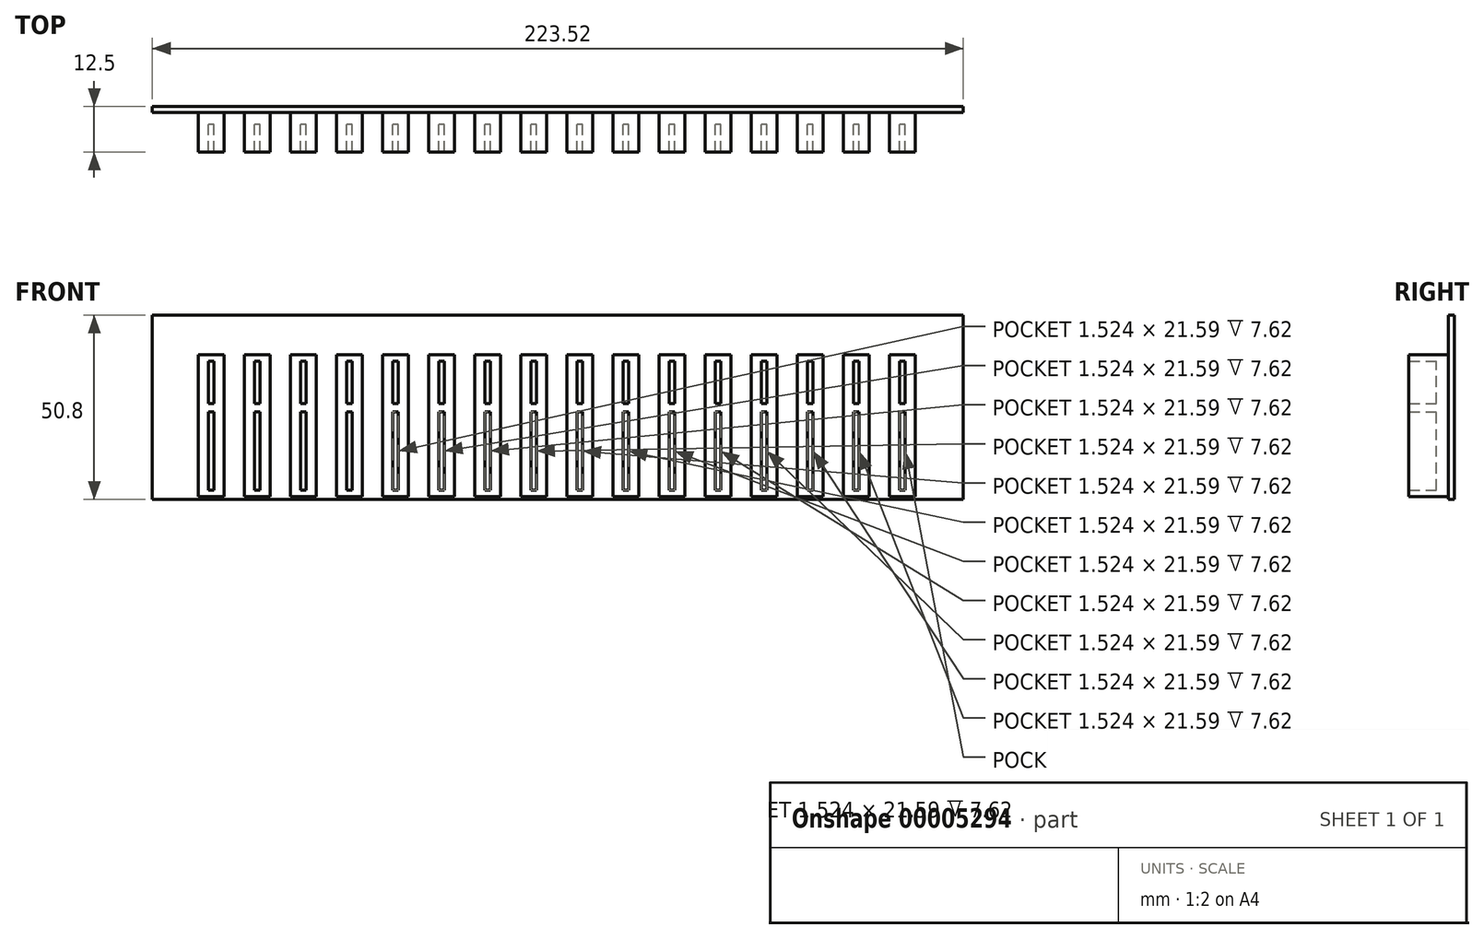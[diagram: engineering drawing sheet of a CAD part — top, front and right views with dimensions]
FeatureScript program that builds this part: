
annotation { "Feature Type Name" : "Feature", "Feature Type Description" : "" }
export const myFeature = defineFeature(function(context is Context, id is Id, definition is map)
    precondition{}
    {
        {
            var Q0;
            Q0=qCreatedBy(makeId("Front.planeOp"),FACE);
            var sketch = newSketch(context, id + "F0", { "sketchPlane" : qUnion([Q0])});
            skLineSegment(sketch, "E0.bottom", {"start": v(-92.93, 33.46) * mm, "end": v(130.6, 33.46) * mm});
            skLineSegment(sketch, "E0.top", {"start": v(-92.93, -17.34) * mm, "end": v(130.6, -17.34) * mm});
            skLineSegment(sketch, "E0.left", {"start": v(-92.93, 33.46) * mm, "end": v(-92.93, -17.34) * mm});
            skLineSegment(sketch, "E0.right", {"start": v(130.6, 33.46) * mm, "end": v(130.6, -17.34) * mm});
            skSolve(sketch);
        }
        {
            var Q0;
            Q0 = qSketchRegion(id + "F0", true);
            extrude(context, id + "F1", {"entities" : qUnion([Q0]), "depth" : 1.57 * mm});
        }
        {
            var Q0;
            Q0=makeQuery(id+"F1.opExtrude","CAP_FACE",FACE,{"disambiguationData":[OSD([sQuery(id+"F0.wireOp",EDGE,"E0.bottom"),sQuery(id+"F0.wireOp",EDGE,"E0.top"),sQuery(id+"F0.wireOp",EDGE,"E0.left"),sQuery(id+"F0.wireOp",EDGE,"E0.right")])],"isStart":false});
            var sketch = newSketch(context, id + "F2", { "sketchPlane" : qUnion([Q0])});
            skLineSegment(sketch, "E1", {"start": v(-80.23, 22.54) * mm, "end": v(-80.23, -16.58) * mm});
            skLineSegment(sketch, "E2", {"start": v(-80.23, 2.98) * mm, "end": v(-92.93, 2.98) * mm});
            skLineSegment(sketch, "E3", {"start": v(-80.23, 22.54) * mm, "end": v(-73.11, 22.54) * mm});
            skLineSegment(sketch, "E4", {"start": v(-73.11, 22.54) * mm, "end": v(-73.11, -16.58) * mm});
            skLineSegment(sketch, "E5", {"start": v(-73.11, -16.58) * mm, "end": v(-80.23, -16.58) * mm});
            skLineSegment(sketch, "E6", {"start": v(-76.67, 20.76) * mm, "end": v(-77.43, 20.76) * mm});
            skPoint(sketch, "E6.startSnap0", {"position": v(-76.67, 22.54) * mm});
            skLineSegment(sketch, "E7", {"start": v(-77.43, 20.76) * mm, "end": v(-77.43, 9.08) * mm});
            skLineSegment(sketch, "E8", {"start": v(-77.43, 9.08) * mm, "end": v(-75.9, 9.08) * mm});
            skLineSegment(sketch, "E9", {"start": v(-75.9, 9.08) * mm, "end": v(-75.9, 20.76) * mm});
            skLineSegment(sketch, "E10", {"start": v(-75.9, 20.76) * mm, "end": v(-76.67, 20.76) * mm});
            skLineSegment(sketch, "E11", {"start": v(-76.67, 20.76) * mm, "end": v(-76.67, 22.54) * mm});
            skLineSegment(sketch, "E12", {"start": v(-76.67, -16.58) * mm, "end": v(-76.67, -14.8) * mm});
            skLineSegment(sketch, "E13", {"start": v(-76.67, -14.8) * mm, "end": v(-77.43, -14.8) * mm});
            skLineSegment(sketch, "E14", {"start": v(-77.43, -14.8) * mm, "end": v(-77.43, 6.8) * mm});
            skLineSegment(sketch, "E15", {"start": v(-77.43, 6.8) * mm, "end": v(-75.9, 6.8) * mm});
            skLineSegment(sketch, "E16", {"start": v(-75.9, 6.8) * mm, "end": v(-75.9, -14.8) * mm});
            skLineSegment(sketch, "E17", {"start": v(-75.9, -14.8) * mm, "end": v(-76.67, -14.8) * mm});
            skLineSegment(sketch, "E18.1.0.0", {"start": v(-64.73, -14.8) * mm, "end": v(-64.73, 6.8) * mm});
            skPoint(sketch, "E18.1.0.1", {"position": v(-63.97, 22.54) * mm});
            skLineSegment(sketch, "E18.1.0.2", {"start": v(-63.2, 6.8) * mm, "end": v(-63.2, -14.8) * mm});
            skLineSegment(sketch, "E18.1.0.3", {"start": v(-67.53, 22.54) * mm, "end": v(-67.53, -16.58) * mm});
            skLineSegment(sketch, "E18.1.0.4", {"start": v(-67.53, 22.54) * mm, "end": v(-60.41, 22.54) * mm});
            skLineSegment(sketch, "E18.1.0.5", {"start": v(-60.41, 22.54) * mm, "end": v(-60.41, -16.58) * mm});
            skLineSegment(sketch, "E18.1.0.6", {"start": v(-60.41, -16.58) * mm, "end": v(-67.53, -16.58) * mm});
            skLineSegment(sketch, "E18.1.0.7", {"start": v(-63.2, 9.08) * mm, "end": v(-63.2, 20.76) * mm});
            skLineSegment(sketch, "E18.1.0.8", {"start": v(-64.73, 20.76) * mm, "end": v(-64.73, 9.08) * mm});
            skLineSegment(sketch, "E18.1.0.9", {"start": v(-63.97, -16.58) * mm, "end": v(-63.97, -14.8) * mm});
            skLineSegment(sketch, "E18.1.0.10", {"start": v(-64.73, 6.8) * mm, "end": v(-63.2, 6.8) * mm});
            skLineSegment(sketch, "E18.1.0.11", {"start": v(-63.97, 20.76) * mm, "end": v(-63.97, 22.54) * mm});
            skLineSegment(sketch, "E18.1.0.12", {"start": v(-64.73, 9.08) * mm, "end": v(-63.2, 9.08) * mm});
            skLineSegment(sketch, "E18.1.0.13", {"start": v(-63.97, -14.8) * mm, "end": v(-64.73, -14.8) * mm});
            skLineSegment(sketch, "E18.1.0.14", {"start": v(-63.2, -14.8) * mm, "end": v(-63.97, -14.8) * mm});
            skLineSegment(sketch, "E18.1.0.15", {"start": v(-63.2, 20.76) * mm, "end": v(-63.97, 20.76) * mm});
            skLineSegment(sketch, "E18.1.0.16", {"start": v(-63.97, 20.76) * mm, "end": v(-64.73, 20.76) * mm});
            skLineSegment(sketch, "E18.2.0.0", {"start": v(-52.03, -14.8) * mm, "end": v(-52.03, 6.8) * mm});
            skPoint(sketch, "E18.2.0.1", {"position": v(-51.27, 22.54) * mm});
            skLineSegment(sketch, "E18.2.0.2", {"start": v(-50.5, 6.8) * mm, "end": v(-50.5, -14.8) * mm});
            skLineSegment(sketch, "E18.2.0.3", {"start": v(-54.83, 22.54) * mm, "end": v(-54.83, -16.58) * mm});
            skLineSegment(sketch, "E18.2.0.4", {"start": v(-54.83, 22.54) * mm, "end": v(-47.71, 22.54) * mm});
            skLineSegment(sketch, "E18.2.0.5", {"start": v(-47.71, 22.54) * mm, "end": v(-47.71, -16.58) * mm});
            skLineSegment(sketch, "E18.2.0.6", {"start": v(-47.71, -16.58) * mm, "end": v(-54.83, -16.58) * mm});
            skLineSegment(sketch, "E18.2.0.7", {"start": v(-50.5, 9.08) * mm, "end": v(-50.5, 20.76) * mm});
            skLineSegment(sketch, "E18.2.0.8", {"start": v(-52.03, 20.76) * mm, "end": v(-52.03, 9.08) * mm});
            skLineSegment(sketch, "E18.2.0.9", {"start": v(-51.27, -16.58) * mm, "end": v(-51.27, -14.8) * mm});
            skLineSegment(sketch, "E18.2.0.10", {"start": v(-52.03, 6.8) * mm, "end": v(-50.5, 6.8) * mm});
            skLineSegment(sketch, "E18.2.0.11", {"start": v(-51.27, 20.76) * mm, "end": v(-51.27, 22.54) * mm});
            skLineSegment(sketch, "E18.2.0.12", {"start": v(-52.03, 9.08) * mm, "end": v(-50.5, 9.08) * mm});
            skLineSegment(sketch, "E18.2.0.13", {"start": v(-51.27, -14.8) * mm, "end": v(-52.03, -14.8) * mm});
            skLineSegment(sketch, "E18.2.0.14", {"start": v(-50.5, -14.8) * mm, "end": v(-51.27, -14.8) * mm});
            skLineSegment(sketch, "E18.2.0.15", {"start": v(-50.5, 20.76) * mm, "end": v(-51.27, 20.76) * mm});
            skLineSegment(sketch, "E18.2.0.16", {"start": v(-51.27, 20.76) * mm, "end": v(-52.03, 20.76) * mm});
            skLineSegment(sketch, "E18.3.0.0", {"start": v(-39.33, -14.8) * mm, "end": v(-39.33, 6.8) * mm});
            skPoint(sketch, "E18.3.0.1", {"position": v(-38.57, 22.54) * mm});
            skLineSegment(sketch, "E18.3.0.2", {"start": v(-37.8, 6.8) * mm, "end": v(-37.8, -14.8) * mm});
            skLineSegment(sketch, "E18.3.0.3", {"start": v(-42.13, 22.54) * mm, "end": v(-42.13, -16.58) * mm});
            skLineSegment(sketch, "E18.3.0.4", {"start": v(-42.13, 22.54) * mm, "end": v(-35.01, 22.54) * mm});
            skLineSegment(sketch, "E18.3.0.5", {"start": v(-35.01, 22.54) * mm, "end": v(-35.01, -16.58) * mm});
            skLineSegment(sketch, "E18.3.0.6", {"start": v(-35.01, -16.58) * mm, "end": v(-42.13, -16.58) * mm});
            skLineSegment(sketch, "E18.3.0.7", {"start": v(-37.8, 9.08) * mm, "end": v(-37.8, 20.76) * mm});
            skLineSegment(sketch, "E18.3.0.8", {"start": v(-39.33, 20.76) * mm, "end": v(-39.33, 9.08) * mm});
            skLineSegment(sketch, "E18.3.0.9", {"start": v(-38.57, -16.58) * mm, "end": v(-38.57, -14.8) * mm});
            skLineSegment(sketch, "E18.3.0.10", {"start": v(-39.33, 6.8) * mm, "end": v(-37.8, 6.8) * mm});
            skLineSegment(sketch, "E18.3.0.11", {"start": v(-38.57, 20.76) * mm, "end": v(-38.57, 22.54) * mm});
            skLineSegment(sketch, "E18.3.0.12", {"start": v(-39.33, 9.08) * mm, "end": v(-37.8, 9.08) * mm});
            skLineSegment(sketch, "E18.3.0.13", {"start": v(-38.57, -14.8) * mm, "end": v(-39.33, -14.8) * mm});
            skLineSegment(sketch, "E18.3.0.14", {"start": v(-37.8, -14.8) * mm, "end": v(-38.57, -14.8) * mm});
            skLineSegment(sketch, "E18.3.0.15", {"start": v(-37.8, 20.76) * mm, "end": v(-38.57, 20.76) * mm});
            skLineSegment(sketch, "E18.3.0.16", {"start": v(-38.57, 20.76) * mm, "end": v(-39.33, 20.76) * mm});
            skLineSegment(sketch, "E18.4.0.0", {"start": v(-26.63, -14.8) * mm, "end": v(-26.63, 6.8) * mm});
            skPoint(sketch, "E18.4.0.1", {"position": v(-25.87, 22.54) * mm});
            skLineSegment(sketch, "E18.4.0.2", {"start": v(-25.1, 6.8) * mm, "end": v(-25.1, -14.8) * mm});
            skLineSegment(sketch, "E18.4.0.3", {"start": v(-29.43, 22.54) * mm, "end": v(-29.43, -16.58) * mm});
            skLineSegment(sketch, "E18.4.0.4", {"start": v(-29.43, 22.54) * mm, "end": v(-22.31, 22.54) * mm});
            skLineSegment(sketch, "E18.4.0.5", {"start": v(-22.31, 22.54) * mm, "end": v(-22.31, -16.58) * mm});
            skLineSegment(sketch, "E18.4.0.6", {"start": v(-22.31, -16.58) * mm, "end": v(-29.43, -16.58) * mm});
            skLineSegment(sketch, "E18.4.0.7", {"start": v(-25.1, 9.08) * mm, "end": v(-25.1, 20.76) * mm});
            skLineSegment(sketch, "E18.4.0.8", {"start": v(-26.63, 20.76) * mm, "end": v(-26.63, 9.08) * mm});
            skLineSegment(sketch, "E18.4.0.9", {"start": v(-25.87, -16.58) * mm, "end": v(-25.87, -14.8) * mm});
            skLineSegment(sketch, "E18.4.0.10", {"start": v(-26.63, 6.8) * mm, "end": v(-25.1, 6.8) * mm});
            skLineSegment(sketch, "E18.4.0.11", {"start": v(-25.87, 20.76) * mm, "end": v(-25.87, 22.54) * mm});
            skLineSegment(sketch, "E18.4.0.12", {"start": v(-26.63, 9.08) * mm, "end": v(-25.1, 9.08) * mm});
            skLineSegment(sketch, "E18.4.0.13", {"start": v(-25.87, -14.8) * mm, "end": v(-26.63, -14.8) * mm});
            skLineSegment(sketch, "E18.4.0.14", {"start": v(-25.1, -14.8) * mm, "end": v(-25.87, -14.8) * mm});
            skLineSegment(sketch, "E18.4.0.15", {"start": v(-25.1, 20.76) * mm, "end": v(-25.87, 20.76) * mm});
            skLineSegment(sketch, "E18.4.0.16", {"start": v(-25.87, 20.76) * mm, "end": v(-26.63, 20.76) * mm});
            skLineSegment(sketch, "E18.5.0.0", {"start": v(-13.93, -14.8) * mm, "end": v(-13.93, 6.8) * mm});
            skPoint(sketch, "E18.5.0.1", {"position": v(-13.17, 22.54) * mm});
            skLineSegment(sketch, "E18.5.0.2", {"start": v(-12.4, 6.8) * mm, "end": v(-12.4, -14.8) * mm});
            skLineSegment(sketch, "E18.5.0.3", {"start": v(-16.73, 22.54) * mm, "end": v(-16.73, -16.58) * mm});
            skLineSegment(sketch, "E18.5.0.4", {"start": v(-16.73, 22.54) * mm, "end": v(-9.61, 22.54) * mm});
            skLineSegment(sketch, "E18.5.0.5", {"start": v(-9.61, 22.54) * mm, "end": v(-9.61, -16.58) * mm});
            skLineSegment(sketch, "E18.5.0.6", {"start": v(-9.61, -16.58) * mm, "end": v(-16.73, -16.58) * mm});
            skLineSegment(sketch, "E18.5.0.7", {"start": v(-12.4, 9.08) * mm, "end": v(-12.4, 20.76) * mm});
            skLineSegment(sketch, "E18.5.0.8", {"start": v(-13.93, 20.76) * mm, "end": v(-13.93, 9.08) * mm});
            skLineSegment(sketch, "E18.5.0.9", {"start": v(-13.17, -16.58) * mm, "end": v(-13.17, -14.8) * mm});
            skLineSegment(sketch, "E18.5.0.10", {"start": v(-13.93, 6.8) * mm, "end": v(-12.4, 6.8) * mm});
            skLineSegment(sketch, "E18.5.0.11", {"start": v(-13.17, 20.76) * mm, "end": v(-13.17, 22.54) * mm});
            skLineSegment(sketch, "E18.5.0.12", {"start": v(-13.93, 9.08) * mm, "end": v(-12.4, 9.08) * mm});
            skLineSegment(sketch, "E18.5.0.13", {"start": v(-13.17, -14.8) * mm, "end": v(-13.93, -14.8) * mm});
            skLineSegment(sketch, "E18.5.0.14", {"start": v(-12.4, -14.8) * mm, "end": v(-13.17, -14.8) * mm});
            skLineSegment(sketch, "E18.5.0.15", {"start": v(-12.4, 20.76) * mm, "end": v(-13.17, 20.76) * mm});
            skLineSegment(sketch, "E18.5.0.16", {"start": v(-13.17, 20.76) * mm, "end": v(-13.93, 20.76) * mm});
            skLineSegment(sketch, "E18.6.0.0", {"start": v(-1.23, -14.8) * mm, "end": v(-1.23, 6.8) * mm});
            skPoint(sketch, "E18.6.0.1", {"position": v(-0.47, 22.54) * mm});
            skLineSegment(sketch, "E18.6.0.2", {"start": v(0.3, 6.8) * mm, "end": v(0.3, -14.8) * mm});
            skLineSegment(sketch, "E18.6.0.3", {"start": v(-4.03, 22.54) * mm, "end": v(-4.03, -16.58) * mm});
            skLineSegment(sketch, "E18.6.0.4", {"start": v(-4.03, 22.54) * mm, "end": v(3.09, 22.54) * mm});
            skLineSegment(sketch, "E18.6.0.5", {"start": v(3.09, 22.54) * mm, "end": v(3.09, -16.58) * mm});
            skLineSegment(sketch, "E18.6.0.6", {"start": v(3.09, -16.58) * mm, "end": v(-4.03, -16.58) * mm});
            skLineSegment(sketch, "E18.6.0.7", {"start": v(0.3, 9.08) * mm, "end": v(0.3, 20.76) * mm});
            skLineSegment(sketch, "E18.6.0.8", {"start": v(-1.23, 20.76) * mm, "end": v(-1.23, 9.08) * mm});
            skLineSegment(sketch, "E18.6.0.9", {"start": v(-0.47, -16.58) * mm, "end": v(-0.47, -14.8) * mm});
            skLineSegment(sketch, "E18.6.0.10", {"start": v(-1.23, 6.8) * mm, "end": v(0.3, 6.8) * mm});
            skLineSegment(sketch, "E18.6.0.11", {"start": v(-0.47, 20.76) * mm, "end": v(-0.47, 22.54) * mm});
            skLineSegment(sketch, "E18.6.0.12", {"start": v(-1.23, 9.08) * mm, "end": v(0.3, 9.08) * mm});
            skLineSegment(sketch, "E18.6.0.13", {"start": v(-0.47, -14.8) * mm, "end": v(-1.23, -14.8) * mm});
            skLineSegment(sketch, "E18.6.0.14", {"start": v(0.3, -14.8) * mm, "end": v(-0.47, -14.8) * mm});
            skLineSegment(sketch, "E18.6.0.15", {"start": v(0.3, 20.76) * mm, "end": v(-0.47, 20.76) * mm});
            skLineSegment(sketch, "E18.6.0.16", {"start": v(-0.47, 20.76) * mm, "end": v(-1.23, 20.76) * mm});
            skLineSegment(sketch, "E18.7.0.0", {"start": v(11.47, -14.8) * mm, "end": v(11.47, 6.8) * mm});
            skPoint(sketch, "E18.7.0.1", {"position": v(12.23, 22.54) * mm});
            skLineSegment(sketch, "E18.7.0.2", {"start": v(13, 6.8) * mm, "end": v(13, -14.8) * mm});
            skLineSegment(sketch, "E18.7.0.3", {"start": v(8.67, 22.54) * mm, "end": v(8.67, -16.58) * mm});
            skLineSegment(sketch, "E18.7.0.4", {"start": v(8.67, 22.54) * mm, "end": v(15.79, 22.54) * mm});
            skLineSegment(sketch, "E18.7.0.5", {"start": v(15.79, 22.54) * mm, "end": v(15.79, -16.58) * mm});
            skLineSegment(sketch, "E18.7.0.6", {"start": v(15.79, -16.58) * mm, "end": v(8.67, -16.58) * mm});
            skLineSegment(sketch, "E18.7.0.7", {"start": v(13, 9.08) * mm, "end": v(13, 20.76) * mm});
            skLineSegment(sketch, "E18.7.0.8", {"start": v(11.47, 20.76) * mm, "end": v(11.47, 9.08) * mm});
            skLineSegment(sketch, "E18.7.0.9", {"start": v(12.23, -16.58) * mm, "end": v(12.23, -14.8) * mm});
            skLineSegment(sketch, "E18.7.0.10", {"start": v(11.47, 6.8) * mm, "end": v(13, 6.8) * mm});
            skLineSegment(sketch, "E18.7.0.11", {"start": v(12.23, 20.76) * mm, "end": v(12.23, 22.54) * mm});
            skLineSegment(sketch, "E18.7.0.12", {"start": v(11.47, 9.08) * mm, "end": v(13, 9.08) * mm});
            skLineSegment(sketch, "E18.7.0.13", {"start": v(12.23, -14.8) * mm, "end": v(11.47, -14.8) * mm});
            skLineSegment(sketch, "E18.7.0.14", {"start": v(13, -14.8) * mm, "end": v(12.23, -14.8) * mm});
            skLineSegment(sketch, "E18.7.0.15", {"start": v(13, 20.76) * mm, "end": v(12.23, 20.76) * mm});
            skLineSegment(sketch, "E18.7.0.16", {"start": v(12.23, 20.76) * mm, "end": v(11.47, 20.76) * mm});
            skLineSegment(sketch, "E18.8.0.0", {"start": v(24.17, -14.8) * mm, "end": v(24.17, 6.8) * mm});
            skPoint(sketch, "E18.8.0.1", {"position": v(24.93, 22.54) * mm});
            skLineSegment(sketch, "E18.8.0.2", {"start": v(25.7, 6.8) * mm, "end": v(25.7, -14.8) * mm});
            skLineSegment(sketch, "E18.8.0.3", {"start": v(21.37, 22.54) * mm, "end": v(21.37, -16.58) * mm});
            skLineSegment(sketch, "E18.8.0.4", {"start": v(21.37, 22.54) * mm, "end": v(28.49, 22.54) * mm});
            skLineSegment(sketch, "E18.8.0.5", {"start": v(28.49, 22.54) * mm, "end": v(28.49, -16.58) * mm});
            skLineSegment(sketch, "E18.8.0.6", {"start": v(28.49, -16.58) * mm, "end": v(21.37, -16.58) * mm});
            skLineSegment(sketch, "E18.8.0.7", {"start": v(25.7, 9.08) * mm, "end": v(25.7, 20.76) * mm});
            skLineSegment(sketch, "E18.8.0.8", {"start": v(24.17, 20.76) * mm, "end": v(24.17, 9.08) * mm});
            skLineSegment(sketch, "E18.8.0.9", {"start": v(24.93, -16.58) * mm, "end": v(24.93, -14.8) * mm});
            skLineSegment(sketch, "E18.8.0.10", {"start": v(24.17, 6.8) * mm, "end": v(25.7, 6.8) * mm});
            skLineSegment(sketch, "E18.8.0.11", {"start": v(24.93, 20.76) * mm, "end": v(24.93, 22.54) * mm});
            skLineSegment(sketch, "E18.8.0.12", {"start": v(24.17, 9.08) * mm, "end": v(25.7, 9.08) * mm});
            skLineSegment(sketch, "E18.8.0.13", {"start": v(24.93, -14.8) * mm, "end": v(24.17, -14.8) * mm});
            skLineSegment(sketch, "E18.8.0.14", {"start": v(25.7, -14.8) * mm, "end": v(24.93, -14.8) * mm});
            skLineSegment(sketch, "E18.8.0.15", {"start": v(25.7, 20.76) * mm, "end": v(24.93, 20.76) * mm});
            skLineSegment(sketch, "E18.8.0.16", {"start": v(24.93, 20.76) * mm, "end": v(24.17, 20.76) * mm});
            skLineSegment(sketch, "E18.9.0.0", {"start": v(36.87, -14.8) * mm, "end": v(36.87, 6.8) * mm});
            skPoint(sketch, "E18.9.0.1", {"position": v(37.63, 22.54) * mm});
            skLineSegment(sketch, "E18.9.0.2", {"start": v(38.4, 6.8) * mm, "end": v(38.4, -14.8) * mm});
            skLineSegment(sketch, "E18.9.0.3", {"start": v(34.07, 22.54) * mm, "end": v(34.07, -16.58) * mm});
            skLineSegment(sketch, "E18.9.0.4", {"start": v(34.07, 22.54) * mm, "end": v(41.19, 22.54) * mm});
            skLineSegment(sketch, "E18.9.0.5", {"start": v(41.19, 22.54) * mm, "end": v(41.19, -16.58) * mm});
            skLineSegment(sketch, "E18.9.0.6", {"start": v(41.19, -16.58) * mm, "end": v(34.07, -16.58) * mm});
            skLineSegment(sketch, "E18.9.0.7", {"start": v(38.4, 9.08) * mm, "end": v(38.4, 20.76) * mm});
            skLineSegment(sketch, "E18.9.0.8", {"start": v(36.87, 20.76) * mm, "end": v(36.87, 9.08) * mm});
            skLineSegment(sketch, "E18.9.0.9", {"start": v(37.63, -16.58) * mm, "end": v(37.63, -14.8) * mm});
            skLineSegment(sketch, "E18.9.0.10", {"start": v(36.87, 6.8) * mm, "end": v(38.4, 6.8) * mm});
            skLineSegment(sketch, "E18.9.0.11", {"start": v(37.63, 20.76) * mm, "end": v(37.63, 22.54) * mm});
            skLineSegment(sketch, "E18.9.0.12", {"start": v(36.87, 9.08) * mm, "end": v(38.4, 9.08) * mm});
            skLineSegment(sketch, "E18.9.0.13", {"start": v(37.63, -14.8) * mm, "end": v(36.87, -14.8) * mm});
            skLineSegment(sketch, "E18.9.0.14", {"start": v(38.4, -14.8) * mm, "end": v(37.63, -14.8) * mm});
            skLineSegment(sketch, "E18.9.0.15", {"start": v(38.4, 20.76) * mm, "end": v(37.63, 20.76) * mm});
            skLineSegment(sketch, "E18.9.0.16", {"start": v(37.63, 20.76) * mm, "end": v(36.87, 20.76) * mm});
            skLineSegment(sketch, "E18.10.0.0", {"start": v(49.57, -14.8) * mm, "end": v(49.57, 6.8) * mm});
            skPoint(sketch, "E18.10.0.1", {"position": v(50.33, 22.54) * mm});
            skLineSegment(sketch, "E18.10.0.2", {"start": v(51.1, 6.8) * mm, "end": v(51.1, -14.8) * mm});
            skLineSegment(sketch, "E18.10.0.3", {"start": v(46.77, 22.54) * mm, "end": v(46.77, -16.58) * mm});
            skLineSegment(sketch, "E18.10.0.4", {"start": v(46.77, 22.54) * mm, "end": v(53.89, 22.54) * mm});
            skLineSegment(sketch, "E18.10.0.5", {"start": v(53.89, 22.54) * mm, "end": v(53.89, -16.58) * mm});
            skLineSegment(sketch, "E18.10.0.6", {"start": v(53.89, -16.58) * mm, "end": v(46.77, -16.58) * mm});
            skLineSegment(sketch, "E18.10.0.7", {"start": v(51.1, 9.08) * mm, "end": v(51.1, 20.76) * mm});
            skLineSegment(sketch, "E18.10.0.8", {"start": v(49.57, 20.76) * mm, "end": v(49.57, 9.08) * mm});
            skLineSegment(sketch, "E18.10.0.9", {"start": v(50.33, -16.58) * mm, "end": v(50.33, -14.8) * mm});
            skLineSegment(sketch, "E18.10.0.10", {"start": v(49.57, 6.8) * mm, "end": v(51.1, 6.8) * mm});
            skLineSegment(sketch, "E18.10.0.11", {"start": v(50.33, 20.76) * mm, "end": v(50.33, 22.54) * mm});
            skLineSegment(sketch, "E18.10.0.12", {"start": v(49.57, 9.08) * mm, "end": v(51.1, 9.08) * mm});
            skLineSegment(sketch, "E18.10.0.13", {"start": v(50.33, -14.8) * mm, "end": v(49.57, -14.8) * mm});
            skLineSegment(sketch, "E18.10.0.14", {"start": v(51.1, -14.8) * mm, "end": v(50.33, -14.8) * mm});
            skLineSegment(sketch, "E18.10.0.15", {"start": v(51.1, 20.76) * mm, "end": v(50.33, 20.76) * mm});
            skLineSegment(sketch, "E18.10.0.16", {"start": v(50.33, 20.76) * mm, "end": v(49.57, 20.76) * mm});
            skLineSegment(sketch, "E18.11.0.0", {"start": v(62.27, -14.8) * mm, "end": v(62.27, 6.8) * mm});
            skPoint(sketch, "E18.11.0.1", {"position": v(63.03, 22.54) * mm});
            skLineSegment(sketch, "E18.11.0.2", {"start": v(63.8, 6.8) * mm, "end": v(63.8, -14.8) * mm});
            skLineSegment(sketch, "E18.11.0.3", {"start": v(59.47, 22.54) * mm, "end": v(59.47, -16.58) * mm});
            skLineSegment(sketch, "E18.11.0.4", {"start": v(59.47, 22.54) * mm, "end": v(66.59, 22.54) * mm});
            skLineSegment(sketch, "E18.11.0.5", {"start": v(66.59, 22.54) * mm, "end": v(66.59, -16.58) * mm});
            skLineSegment(sketch, "E18.11.0.6", {"start": v(66.59, -16.58) * mm, "end": v(59.47, -16.58) * mm});
            skLineSegment(sketch, "E18.11.0.7", {"start": v(63.8, 9.08) * mm, "end": v(63.8, 20.76) * mm});
            skLineSegment(sketch, "E18.11.0.8", {"start": v(62.27, 20.76) * mm, "end": v(62.27, 9.08) * mm});
            skLineSegment(sketch, "E18.11.0.9", {"start": v(63.03, -16.58) * mm, "end": v(63.03, -14.8) * mm});
            skLineSegment(sketch, "E18.11.0.10", {"start": v(62.27, 6.8) * mm, "end": v(63.8, 6.8) * mm});
            skLineSegment(sketch, "E18.11.0.11", {"start": v(63.03, 20.76) * mm, "end": v(63.03, 22.54) * mm});
            skLineSegment(sketch, "E18.11.0.12", {"start": v(62.27, 9.08) * mm, "end": v(63.8, 9.08) * mm});
            skLineSegment(sketch, "E18.11.0.13", {"start": v(63.03, -14.8) * mm, "end": v(62.27, -14.8) * mm});
            skLineSegment(sketch, "E18.11.0.14", {"start": v(63.8, -14.8) * mm, "end": v(63.03, -14.8) * mm});
            skLineSegment(sketch, "E18.11.0.15", {"start": v(63.8, 20.76) * mm, "end": v(63.03, 20.76) * mm});
            skLineSegment(sketch, "E18.11.0.16", {"start": v(63.03, 20.76) * mm, "end": v(62.27, 20.76) * mm});
            skLineSegment(sketch, "E18.12.0.0", {"start": v(74.97, -14.8) * mm, "end": v(74.97, 6.8) * mm});
            skPoint(sketch, "E18.12.0.1", {"position": v(75.73, 22.54) * mm});
            skLineSegment(sketch, "E18.12.0.2", {"start": v(76.5, 6.8) * mm, "end": v(76.5, -14.8) * mm});
            skLineSegment(sketch, "E18.12.0.3", {"start": v(72.17, 22.54) * mm, "end": v(72.17, -16.58) * mm});
            skLineSegment(sketch, "E18.12.0.4", {"start": v(72.17, 22.54) * mm, "end": v(79.29, 22.54) * mm});
            skLineSegment(sketch, "E18.12.0.5", {"start": v(79.29, 22.54) * mm, "end": v(79.29, -16.58) * mm});
            skLineSegment(sketch, "E18.12.0.6", {"start": v(79.29, -16.58) * mm, "end": v(72.17, -16.58) * mm});
            skLineSegment(sketch, "E18.12.0.7", {"start": v(76.5, 9.08) * mm, "end": v(76.5, 20.76) * mm});
            skLineSegment(sketch, "E18.12.0.8", {"start": v(74.97, 20.76) * mm, "end": v(74.97, 9.08) * mm});
            skLineSegment(sketch, "E18.12.0.9", {"start": v(75.73, -16.58) * mm, "end": v(75.73, -14.8) * mm});
            skLineSegment(sketch, "E18.12.0.10", {"start": v(74.97, 6.8) * mm, "end": v(76.5, 6.8) * mm});
            skLineSegment(sketch, "E18.12.0.11", {"start": v(75.73, 20.76) * mm, "end": v(75.73, 22.54) * mm});
            skLineSegment(sketch, "E18.12.0.12", {"start": v(74.97, 9.08) * mm, "end": v(76.5, 9.08) * mm});
            skLineSegment(sketch, "E18.12.0.13", {"start": v(75.73, -14.8) * mm, "end": v(74.97, -14.8) * mm});
            skLineSegment(sketch, "E18.12.0.14", {"start": v(76.5, -14.8) * mm, "end": v(75.73, -14.8) * mm});
            skLineSegment(sketch, "E18.12.0.15", {"start": v(76.5, 20.76) * mm, "end": v(75.73, 20.76) * mm});
            skLineSegment(sketch, "E18.12.0.16", {"start": v(75.73, 20.76) * mm, "end": v(74.97, 20.76) * mm});
            skLineSegment(sketch, "E18.13.0.0", {"start": v(87.67, -14.8) * mm, "end": v(87.67, 6.8) * mm});
            skPoint(sketch, "E18.13.0.1", {"position": v(88.43, 22.54) * mm});
            skLineSegment(sketch, "E18.13.0.2", {"start": v(89.2, 6.8) * mm, "end": v(89.2, -14.8) * mm});
            skLineSegment(sketch, "E18.13.0.3", {"start": v(84.87, 22.54) * mm, "end": v(84.87, -16.58) * mm});
            skLineSegment(sketch, "E18.13.0.4", {"start": v(84.87, 22.54) * mm, "end": v(91.99, 22.54) * mm});
            skLineSegment(sketch, "E18.13.0.5", {"start": v(91.99, 22.54) * mm, "end": v(91.99, -16.58) * mm});
            skLineSegment(sketch, "E18.13.0.6", {"start": v(91.99, -16.58) * mm, "end": v(84.87, -16.58) * mm});
            skLineSegment(sketch, "E18.13.0.7", {"start": v(89.2, 9.08) * mm, "end": v(89.2, 20.76) * mm});
            skLineSegment(sketch, "E18.13.0.8", {"start": v(87.67, 20.76) * mm, "end": v(87.67, 9.08) * mm});
            skLineSegment(sketch, "E18.13.0.9", {"start": v(88.43, -16.58) * mm, "end": v(88.43, -14.8) * mm});
            skLineSegment(sketch, "E18.13.0.10", {"start": v(87.67, 6.8) * mm, "end": v(89.2, 6.8) * mm});
            skLineSegment(sketch, "E18.13.0.11", {"start": v(88.43, 20.76) * mm, "end": v(88.43, 22.54) * mm});
            skLineSegment(sketch, "E18.13.0.12", {"start": v(87.67, 9.08) * mm, "end": v(89.2, 9.08) * mm});
            skLineSegment(sketch, "E18.13.0.13", {"start": v(88.43, -14.8) * mm, "end": v(87.67, -14.8) * mm});
            skLineSegment(sketch, "E18.13.0.14", {"start": v(89.2, -14.8) * mm, "end": v(88.43, -14.8) * mm});
            skLineSegment(sketch, "E18.13.0.15", {"start": v(89.2, 20.76) * mm, "end": v(88.43, 20.76) * mm});
            skLineSegment(sketch, "E18.13.0.16", {"start": v(88.43, 20.76) * mm, "end": v(87.67, 20.76) * mm});
            skLineSegment(sketch, "E18.14.0.0", {"start": v(100.37, -14.8) * mm, "end": v(100.37, 6.8) * mm});
            skPoint(sketch, "E18.14.0.1", {"position": v(101.13, 22.54) * mm});
            skLineSegment(sketch, "E18.14.0.2", {"start": v(101.9, 6.8) * mm, "end": v(101.9, -14.8) * mm});
            skLineSegment(sketch, "E18.14.0.3", {"start": v(97.57, 22.54) * mm, "end": v(97.57, -16.58) * mm});
            skLineSegment(sketch, "E18.14.0.4", {"start": v(97.57, 22.54) * mm, "end": v(104.69, 22.54) * mm});
            skLineSegment(sketch, "E18.14.0.5", {"start": v(104.69, 22.54) * mm, "end": v(104.69, -16.58) * mm});
            skLineSegment(sketch, "E18.14.0.6", {"start": v(104.69, -16.58) * mm, "end": v(97.57, -16.58) * mm});
            skLineSegment(sketch, "E18.14.0.7", {"start": v(101.9, 9.08) * mm, "end": v(101.9, 20.76) * mm});
            skLineSegment(sketch, "E18.14.0.8", {"start": v(100.37, 20.76) * mm, "end": v(100.37, 9.08) * mm});
            skLineSegment(sketch, "E18.14.0.9", {"start": v(101.13, -16.58) * mm, "end": v(101.13, -14.8) * mm});
            skLineSegment(sketch, "E18.14.0.10", {"start": v(100.37, 6.8) * mm, "end": v(101.9, 6.8) * mm});
            skLineSegment(sketch, "E18.14.0.11", {"start": v(101.13, 20.76) * mm, "end": v(101.13, 22.54) * mm});
            skLineSegment(sketch, "E18.14.0.12", {"start": v(100.37, 9.08) * mm, "end": v(101.9, 9.08) * mm});
            skLineSegment(sketch, "E18.14.0.13", {"start": v(101.13, -14.8) * mm, "end": v(100.37, -14.8) * mm});
            skLineSegment(sketch, "E18.14.0.14", {"start": v(101.9, -14.8) * mm, "end": v(101.13, -14.8) * mm});
            skLineSegment(sketch, "E18.14.0.15", {"start": v(101.9, 20.76) * mm, "end": v(101.13, 20.76) * mm});
            skLineSegment(sketch, "E18.14.0.16", {"start": v(101.13, 20.76) * mm, "end": v(100.37, 20.76) * mm});
            skLineSegment(sketch, "E18.15.0.0", {"start": v(113.07, -14.8) * mm, "end": v(113.07, 6.8) * mm});
            skPoint(sketch, "E18.15.0.1", {"position": v(113.83, 22.54) * mm});
            skLineSegment(sketch, "E18.15.0.2", {"start": v(114.6, 6.8) * mm, "end": v(114.6, -14.8) * mm});
            skLineSegment(sketch, "E18.15.0.3", {"start": v(110.27, 22.54) * mm, "end": v(110.27, -16.58) * mm});
            skLineSegment(sketch, "E18.15.0.4", {"start": v(110.27, 22.54) * mm, "end": v(117.39, 22.54) * mm});
            skLineSegment(sketch, "E18.15.0.5", {"start": v(117.39, 22.54) * mm, "end": v(117.39, -16.58) * mm});
            skLineSegment(sketch, "E18.15.0.6", {"start": v(117.39, -16.58) * mm, "end": v(110.27, -16.58) * mm});
            skLineSegment(sketch, "E18.15.0.7", {"start": v(114.6, 9.08) * mm, "end": v(114.6, 20.76) * mm});
            skLineSegment(sketch, "E18.15.0.8", {"start": v(113.07, 20.76) * mm, "end": v(113.07, 9.08) * mm});
            skLineSegment(sketch, "E18.15.0.9", {"start": v(113.83, -16.58) * mm, "end": v(113.83, -14.8) * mm});
            skLineSegment(sketch, "E18.15.0.10", {"start": v(113.07, 6.8) * mm, "end": v(114.6, 6.8) * mm});
            skLineSegment(sketch, "E18.15.0.11", {"start": v(113.83, 20.76) * mm, "end": v(113.83, 22.54) * mm});
            skLineSegment(sketch, "E18.15.0.12", {"start": v(113.07, 9.08) * mm, "end": v(114.6, 9.08) * mm});
            skLineSegment(sketch, "E18.15.0.13", {"start": v(113.83, -14.8) * mm, "end": v(113.07, -14.8) * mm});
            skLineSegment(sketch, "E18.15.0.14", {"start": v(114.6, -14.8) * mm, "end": v(113.83, -14.8) * mm});
            skLineSegment(sketch, "E18.15.0.15", {"start": v(114.6, 20.76) * mm, "end": v(113.83, 20.76) * mm});
            skLineSegment(sketch, "E18.15.0.16", {"start": v(113.83, 20.76) * mm, "end": v(113.07, 20.76) * mm});
            skLineSegment(sketch, "E18.direction1", {"start": v(-80.23, -16.58) * mm, "end": v(-67.53, -16.58) * mm, "construction": true});
            skLineSegment(sketch, "E19", {"start": v(-92.93, 2.98) * mm, "end": v(-92.93, -17.34) * mm});
            skSolve(sketch);
        }
        {
            var Q0;
            {var subQ5=sQuery(id+"F2.wireOp",EDGE,"E4");Q0=makeQuery(id+"F2.imprint","IMPRINT",FACE,{"disambiguationData":[TD([[makeQuery(id+"F2.imprint","IMPRINT",EDGE,{"derivedFrom":subQ5}),-1.0]])]});}
            var Q1;
            Q1=makeQuery(id+"F2.imprint","IMPRINT",FACE,{"disambiguationData":[TD([[makeQuery(id+"F2.imprint","IMPRINT",EDGE,{"derivedFrom":sQuery(id+"F2.wireOp",EDGE,"E18.1.0.0")}),1.0]])]});
            var Q2;
            Q2=makeQuery(id+"F2.imprint","IMPRINT",FACE,{"disambiguationData":[TD([[makeQuery(id+"F2.imprint","IMPRINT",EDGE,{"derivedFrom":sQuery(id+"F2.wireOp",EDGE,"E18.2.0.0")}),1.0]])]});
            var Q3;
            Q3=makeQuery(id+"F2.imprint","IMPRINT",FACE,{"disambiguationData":[TD([[makeQuery(id+"F2.imprint","IMPRINT",EDGE,{"derivedFrom":sQuery(id+"F2.wireOp",EDGE,"E18.3.0.0")}),1.0]])]});
            var Q4;
            Q4=makeQuery(id+"F2.imprint","IMPRINT",FACE,{"disambiguationData":[TD([[makeQuery(id+"F2.imprint","IMPRINT",EDGE,{"derivedFrom":sQuery(id+"F2.wireOp",EDGE,"E18.4.0.0")}),1.0]])]});
            var Q5;
            Q5=makeQuery(id+"F2.imprint","IMPRINT",FACE,{"disambiguationData":[TD([[makeQuery(id+"F2.imprint","IMPRINT",EDGE,{"derivedFrom":sQuery(id+"F2.wireOp",EDGE,"E18.5.0.0")}),1.0]])]});
            var Q6;
            Q6=makeQuery(id+"F2.imprint","IMPRINT",FACE,{"disambiguationData":[TD([[makeQuery(id+"F2.imprint","IMPRINT",EDGE,{"derivedFrom":sQuery(id+"F2.wireOp",EDGE,"E18.6.0.0")}),1.0]])]});
            var Q7;
            Q7=makeQuery(id+"F2.imprint","IMPRINT",FACE,{"disambiguationData":[TD([[makeQuery(id+"F2.imprint","IMPRINT",EDGE,{"derivedFrom":sQuery(id+"F2.wireOp",EDGE,"E18.7.0.0")}),1.0]])]});
            var Q8;
            Q8=makeQuery(id+"F2.imprint","IMPRINT",FACE,{"disambiguationData":[TD([[makeQuery(id+"F2.imprint","IMPRINT",EDGE,{"derivedFrom":sQuery(id+"F2.wireOp",EDGE,"E18.8.0.0")}),1.0]])]});
            var Q9;
            Q9=makeQuery(id+"F2.imprint","IMPRINT",FACE,{"disambiguationData":[TD([[makeQuery(id+"F2.imprint","IMPRINT",EDGE,{"derivedFrom":sQuery(id+"F2.wireOp",EDGE,"E18.9.0.0")}),1.0]])]});
            var Q10;
            Q10=makeQuery(id+"F2.imprint","IMPRINT",FACE,{"disambiguationData":[TD([[makeQuery(id+"F2.imprint","IMPRINT",EDGE,{"derivedFrom":sQuery(id+"F2.wireOp",EDGE,"E18.10.0.0")}),1.0]])]});
            var Q11;
            Q11=makeQuery(id+"F2.imprint","IMPRINT",FACE,{"disambiguationData":[TD([[makeQuery(id+"F2.imprint","IMPRINT",EDGE,{"derivedFrom":sQuery(id+"F2.wireOp",EDGE,"E18.11.0.0")}),1.0]])]});
            var Q12;
            Q12=makeQuery(id+"F2.imprint","IMPRINT",FACE,{"disambiguationData":[TD([[makeQuery(id+"F2.imprint","IMPRINT",EDGE,{"derivedFrom":sQuery(id+"F2.wireOp",EDGE,"E18.12.0.0")}),1.0]])]});
            var Q13;
            Q13=makeQuery(id+"F2.imprint","IMPRINT",FACE,{"disambiguationData":[TD([[makeQuery(id+"F2.imprint","IMPRINT",EDGE,{"derivedFrom":sQuery(id+"F2.wireOp",EDGE,"E18.13.0.0")}),1.0]])]});
            var Q14;
            Q14=makeQuery(id+"F2.imprint","IMPRINT",FACE,{"disambiguationData":[TD([[makeQuery(id+"F2.imprint","IMPRINT",EDGE,{"derivedFrom":sQuery(id+"F2.wireOp",EDGE,"E18.14.0.0")}),1.0]])]});
            var Q15;
            Q15=makeQuery(id+"F2.imprint","IMPRINT",FACE,{"disambiguationData":[TD([[makeQuery(id+"F2.imprint","IMPRINT",EDGE,{"derivedFrom":sQuery(id+"F2.wireOp",EDGE,"E18.15.0.0")}),1.0]])]});
            extrude(context, id + "F3", {"entities" : qUnion([Q0, Q1, Q2, Q3, Q4, Q5, Q6, Q7, Q8, Q9, Q10, Q11, Q12, Q13, Q14, Q15]), "depth" : 10.92 * mm});
        }
        {
            var Q0;
            Q0=makeQuery(id+"F2.imprint","IMPRINT",FACE,{"disambiguationData":[TD([[makeQuery(id+"F2.imprint","IMPRINT",EDGE,{"derivedFrom":sQuery(id+"F2.wireOp",EDGE,"E6")}),1.0]])]});
            var Q1;
            Q1=makeQuery(id+"F2.imprint","IMPRINT",FACE,{"disambiguationData":[TD([[makeQuery(id+"F2.imprint","IMPRINT",EDGE,{"derivedFrom":sQuery(id+"F2.wireOp",EDGE,"E13")}),-1.0]])]});
            var Q2;
            Q2=makeQuery(id+"F2.imprint","IMPRINT",FACE,{"disambiguationData":[TD([[makeQuery(id+"F2.imprint","IMPRINT",EDGE,{"derivedFrom":sQuery(id+"F2.wireOp",EDGE,"E18.1.0.7")}),1.0]])]});
            var Q3;
            Q3=makeQuery(id+"F2.imprint","IMPRINT",FACE,{"disambiguationData":[TD([[makeQuery(id+"F2.imprint","IMPRINT",EDGE,{"derivedFrom":sQuery(id+"F2.wireOp",EDGE,"E18.2.0.7")}),1.0]])]});
            var Q4;
            Q4=makeQuery(id+"F2.imprint","IMPRINT",FACE,{"disambiguationData":[TD([[makeQuery(id+"F2.imprint","IMPRINT",EDGE,{"derivedFrom":sQuery(id+"F2.wireOp",EDGE,"E18.1.0.0")}),-1.0]])]});
            var Q5;
            Q5=makeQuery(id+"F2.imprint","IMPRINT",FACE,{"disambiguationData":[TD([[makeQuery(id+"F2.imprint","IMPRINT",EDGE,{"derivedFrom":sQuery(id+"F2.wireOp",EDGE,"E18.2.0.0")}),-1.0]])]});
            var Q6;
            Q6=makeQuery(id+"F2.imprint","IMPRINT",FACE,{"disambiguationData":[TD([[makeQuery(id+"F2.imprint","IMPRINT",EDGE,{"derivedFrom":sQuery(id+"F2.wireOp",EDGE,"E18.3.0.7")}),1.0]])]});
            var Q7;
            Q7=makeQuery(id+"F2.imprint","IMPRINT",FACE,{"disambiguationData":[TD([[makeQuery(id+"F2.imprint","IMPRINT",EDGE,{"derivedFrom":sQuery(id+"F2.wireOp",EDGE,"E18.3.0.0")}),-1.0]])]});
            var Q8;
            Q8=makeQuery(id+"F2.imprint","IMPRINT",FACE,{"disambiguationData":[TD([[makeQuery(id+"F2.imprint","IMPRINT",EDGE,{"derivedFrom":sQuery(id+"F2.wireOp",EDGE,"E18.4.0.7")}),1.0]])]});
            var Q9;
            Q9=makeQuery(id+"F2.imprint","IMPRINT",FACE,{"disambiguationData":[TD([[makeQuery(id+"F2.imprint","IMPRINT",EDGE,{"derivedFrom":sQuery(id+"F2.wireOp",EDGE,"E18.4.0.0")}),-1.0]])]});
            var Q10;
            Q10=makeQuery(id+"F2.imprint","IMPRINT",FACE,{"disambiguationData":[TD([[makeQuery(id+"F2.imprint","IMPRINT",EDGE,{"derivedFrom":sQuery(id+"F2.wireOp",EDGE,"E18.5.0.0")}),-1.0]])]});
            var Q11;
            Q11=makeQuery(id+"F2.imprint","IMPRINT",FACE,{"disambiguationData":[TD([[makeQuery(id+"F2.imprint","IMPRINT",EDGE,{"derivedFrom":sQuery(id+"F2.wireOp",EDGE,"E18.5.0.7")}),1.0]])]});
            var Q12;
            Q12=makeQuery(id+"F2.imprint","IMPRINT",FACE,{"disambiguationData":[TD([[makeQuery(id+"F2.imprint","IMPRINT",EDGE,{"derivedFrom":sQuery(id+"F2.wireOp",EDGE,"E18.6.0.7")}),1.0]])]});
            var Q13;
            Q13=makeQuery(id+"F2.imprint","IMPRINT",FACE,{"disambiguationData":[TD([[makeQuery(id+"F2.imprint","IMPRINT",EDGE,{"derivedFrom":sQuery(id+"F2.wireOp",EDGE,"E18.7.0.7")}),1.0]])]});
            var Q14;
            Q14=makeQuery(id+"F2.imprint","IMPRINT",FACE,{"disambiguationData":[TD([[makeQuery(id+"F2.imprint","IMPRINT",EDGE,{"derivedFrom":sQuery(id+"F2.wireOp",EDGE,"E18.7.0.0")}),-1.0]])]});
            var Q15;
            Q15=makeQuery(id+"F2.imprint","IMPRINT",FACE,{"disambiguationData":[TD([[makeQuery(id+"F2.imprint","IMPRINT",EDGE,{"derivedFrom":sQuery(id+"F2.wireOp",EDGE,"E18.6.0.0")}),-1.0]])]});
            var Q16;
            Q16=makeQuery(id+"F2.imprint","IMPRINT",FACE,{"disambiguationData":[TD([[makeQuery(id+"F2.imprint","IMPRINT",EDGE,{"derivedFrom":sQuery(id+"F2.wireOp",EDGE,"E18.8.0.7")}),1.0]])]});
            var Q17;
            Q17=makeQuery(id+"F2.imprint","IMPRINT",FACE,{"disambiguationData":[TD([[makeQuery(id+"F2.imprint","IMPRINT",EDGE,{"derivedFrom":sQuery(id+"F2.wireOp",EDGE,"E18.9.0.7")}),1.0]])]});
            var Q18;
            Q18=makeQuery(id+"F2.imprint","IMPRINT",FACE,{"disambiguationData":[TD([[makeQuery(id+"F2.imprint","IMPRINT",EDGE,{"derivedFrom":sQuery(id+"F2.wireOp",EDGE,"E18.10.0.7")}),1.0]])]});
            var Q19;
            Q19=makeQuery(id+"F2.imprint","IMPRINT",FACE,{"disambiguationData":[TD([[makeQuery(id+"F2.imprint","IMPRINT",EDGE,{"derivedFrom":sQuery(id+"F2.wireOp",EDGE,"E18.11.0.7")}),1.0]])]});
            var Q20;
            Q20=makeQuery(id+"F2.imprint","IMPRINT",FACE,{"disambiguationData":[TD([[makeQuery(id+"F2.imprint","IMPRINT",EDGE,{"derivedFrom":sQuery(id+"F2.wireOp",EDGE,"E18.12.0.7")}),1.0]])]});
            var Q21;
            Q21=makeQuery(id+"F2.imprint","IMPRINT",FACE,{"disambiguationData":[TD([[makeQuery(id+"F2.imprint","IMPRINT",EDGE,{"derivedFrom":sQuery(id+"F2.wireOp",EDGE,"E18.12.0.0")}),-1.0]])]});
            var Q22;
            Q22=makeQuery(id+"F2.imprint","IMPRINT",FACE,{"disambiguationData":[TD([[makeQuery(id+"F2.imprint","IMPRINT",EDGE,{"derivedFrom":sQuery(id+"F2.wireOp",EDGE,"E18.11.0.0")}),-1.0]])]});
            var Q23;
            Q23=makeQuery(id+"F2.imprint","IMPRINT",FACE,{"disambiguationData":[TD([[makeQuery(id+"F2.imprint","IMPRINT",EDGE,{"derivedFrom":sQuery(id+"F2.wireOp",EDGE,"E18.10.0.0")}),-1.0]])]});
            var Q24;
            Q24=makeQuery(id+"F2.imprint","IMPRINT",FACE,{"disambiguationData":[TD([[makeQuery(id+"F2.imprint","IMPRINT",EDGE,{"derivedFrom":sQuery(id+"F2.wireOp",EDGE,"E18.9.0.0")}),-1.0]])]});
            var Q25;
            Q25=makeQuery(id+"F2.imprint","IMPRINT",FACE,{"disambiguationData":[TD([[makeQuery(id+"F2.imprint","IMPRINT",EDGE,{"derivedFrom":sQuery(id+"F2.wireOp",EDGE,"E18.8.0.0")}),-1.0]])]});
            var Q26;
            Q26=makeQuery(id+"F2.imprint","IMPRINT",FACE,{"disambiguationData":[TD([[makeQuery(id+"F2.imprint","IMPRINT",EDGE,{"derivedFrom":sQuery(id+"F2.wireOp",EDGE,"E18.13.0.7")}),1.0]])]});
            var Q27;
            Q27=makeQuery(id+"F2.imprint","IMPRINT",FACE,{"disambiguationData":[TD([[makeQuery(id+"F2.imprint","IMPRINT",EDGE,{"derivedFrom":sQuery(id+"F2.wireOp",EDGE,"E18.14.0.7")}),1.0]])]});
            var Q28;
            Q28=makeQuery(id+"F2.imprint","IMPRINT",FACE,{"disambiguationData":[TD([[makeQuery(id+"F2.imprint","IMPRINT",EDGE,{"derivedFrom":sQuery(id+"F2.wireOp",EDGE,"E18.15.0.7")}),1.0]])]});
            var Q29;
            Q29=makeQuery(id+"F2.imprint","IMPRINT",FACE,{"disambiguationData":[TD([[makeQuery(id+"F2.imprint","IMPRINT",EDGE,{"derivedFrom":sQuery(id+"F2.wireOp",EDGE,"E18.15.0.0")}),-1.0]])]});
            var Q30;
            Q30=makeQuery(id+"F2.imprint","IMPRINT",FACE,{"disambiguationData":[TD([[makeQuery(id+"F2.imprint","IMPRINT",EDGE,{"derivedFrom":sQuery(id+"F2.wireOp",EDGE,"E18.14.0.0")}),-1.0]])]});
            var Q31;
            Q31=makeQuery(id+"F2.imprint","IMPRINT",FACE,{"disambiguationData":[TD([[makeQuery(id+"F2.imprint","IMPRINT",EDGE,{"derivedFrom":sQuery(id+"F2.wireOp",EDGE,"E18.13.0.0")}),-1.0]])]});
            extrude(context, id + "F4", {"entities" : qUnion([Q0, Q1, Q2, Q3, Q4, Q5, Q6, Q7, Q8, Q9, Q10, Q11, Q12, Q13, Q14, Q15, Q16, Q17, Q18, Q19, Q20, Q21, Q22, Q23, Q24, Q25, Q26, Q27, Q28, Q29, Q30, Q31]), "operationType" : NewBodyOperationType.ADD, "depth" : 3.3 * mm});
        }
    });
